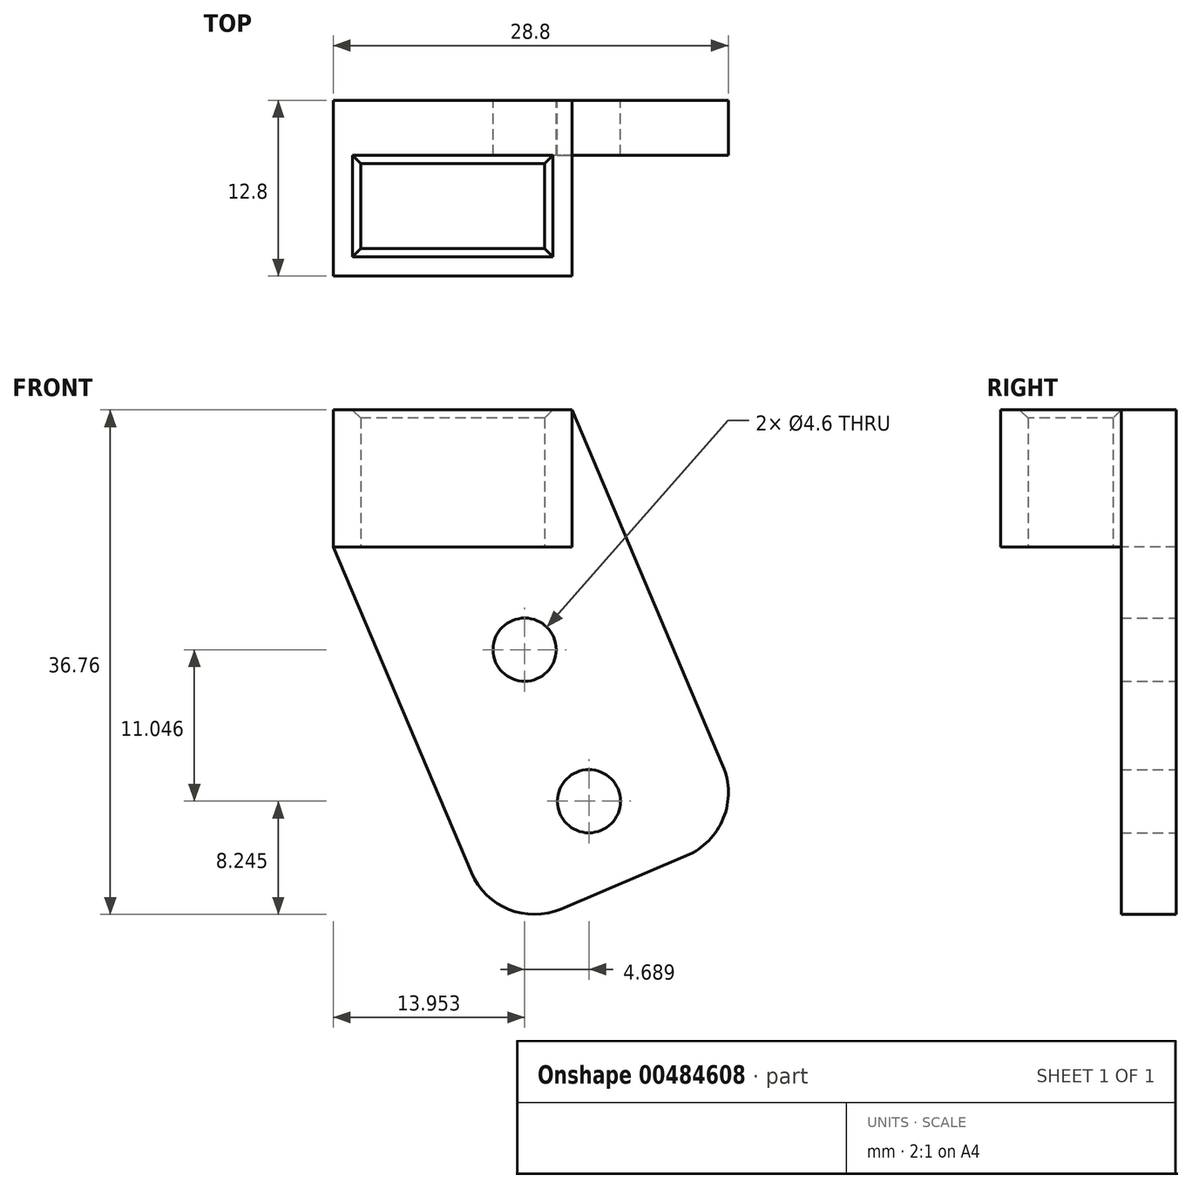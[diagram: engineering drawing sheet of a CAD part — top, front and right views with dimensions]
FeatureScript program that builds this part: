
annotation { "Feature Type Name" : "Feature", "Feature Type Description" : "" }
export const myFeature = defineFeature(function(context is Context, id is Id, definition is map)
    precondition{}
    {
        {
            var Q0;
            Q0=qCreatedBy(makeId("Top.planeOp"),FACE);
            var sketch = newSketch(context, id + "F0", { "sketchPlane" : qUnion([Q0])});
            skLineSegment(sketch, "E0.bottom", {"start": v(-12.09, 6.12) * mm, "end": v(1.31, 6.12) * mm});
            skLineSegment(sketch, "E0.top", {"start": v(-12.09, -0.08) * mm, "end": v(1.31, -0.08) * mm});
            skLineSegment(sketch, "E0.left", {"start": v(-12.09, 6.12) * mm, "end": v(-12.09, -0.08) * mm});
            skLineSegment(sketch, "E0.right", {"start": v(1.31, 6.12) * mm, "end": v(1.31, -0.08) * mm});
            skLineSegment(sketch, "E1.bottom", {"start": v(-14.09, 6.72) * mm, "end": v(3.31, 6.72) * mm});
            skLineSegment(sketch, "E1.top", {"start": v(-14.09, -2.08) * mm, "end": v(3.31, -2.08) * mm});
            skLineSegment(sketch, "E1.left", {"start": v(-14.09, 6.72) * mm, "end": v(-14.09, -2.08) * mm});
            skLineSegment(sketch, "E1.right", {"start": v(3.31, 6.72) * mm, "end": v(3.31, -2.08) * mm});
            skSolve(sketch);
        }
        {
            var Q0;
            Q0=qSketchRegion(id+"F0",true);
            var Q1;
            Q1=makeQuery(id+"F0.imprint","IMPRINT",FACE,{"disambiguationData":[TD([[makeQuery(id+"F0.imprint","IMPRINT",EDGE,{"derivedFrom":sQuery(id+"F0.wireOp",EDGE,"E0.bottom")}),1.0]])]});
            extrude(context, id + "F1", {"entities" : qUnion([Q0, Q1]), "depth" : 10 * mm, "offsetDistance" : 25 * mm});
        }
        {
            var Q0;
            Q0=makeQuery(id+"F1.opExtrude","SWEPT_FACE",FACE,{"disambiguationData":[OSD([sQuery(id+"F0.wireOp",EDGE,"E1.bottom")])]});
            var sketch = newSketch(context, id + "F2", { "sketchPlane" : qUnion([Q0])});
            skLineSegment(sketch, "E2", {"start": v(-3.31, 10) * mm, "end": v(-3.31, 10) * mm});
            skLineSegment(sketch, "E3", {"start": v(-3.31, 10) * mm, "end": v(-16.27, -20.53) * mm});
            skLineSegment(sketch, "E4", {"start": v(2.07, -28.32) * mm, "end": v(14.09, 0) * mm});
            skLineSegment(sketch, "E5", {"start": v(2.07, -28.32) * mm, "end": v(-16.27, -20.53) * mm});
            skPoint(sketch, "E6", {"position": v(0.14, -7.47) * mm});
            skPoint(sketch, "E7", {"position": v(-4.55, -18.52) * mm});
            skSolve(sketch);
        }
        {
            var Q0;
            {var subQ0=sQuery(id+"F2.wireOp",EDGE,"1mkYDBRP-PWp6-GeY6-MU8M-iDzXnznpOOjV.top");Q0=makeQuery(id+"F2.imprint","IMPRINT",FACE,{"disambiguationData":[TD([[makeQuery(id+"F2.imprint","IMPRINT",EDGE,{"derivedFrom":subQ0}),-1.0]])]});}
            var Q1;
            Q1=makeQuery(id+"F2.imprint","IMPRINT",FACE,{"disambiguationData":[TD([[makeQuery(id+"F2.imprint","IMPRINT",EDGE,{"derivedFrom":sQuery(id+"F2.wireOp",EDGE,"f9b377b0-091d-403c-b7d1-5019ea25e836.0.0")}),-1.0]])]});
            var Q2;
            Q2=makeQuery(id+"F2.imprint","IMPRINT",FACE,{"disambiguationData":[TD([[makeQuery(id+"F2.imprint","IMPRINT",EDGE,{"derivedFrom":sQuery(id+"F2.wireOp",EDGE,"E2")}),1.0]])]});
            var Q3;
            {var subQ0=sQuery(id+"F0.wireOp",EDGE,"E1.bottom");Q3=makeQuery(id+"F2.imprint","IMPRINT",FACE,{"disambiguationData":[TD([[makeQuery(id+"F2.imprint","IMPRINT",EDGE,{"derivedFrom":makeQuery(id+"F1.opExtrude","CAP_EDGE",EDGE,{"disambiguationData":[OSD([subQ0])],"isStart":true})}),-1.0]])]});}
            var Q4;
            Q4=makeQuery(id+"F2.imprint","IMPRINT",FACE,{"disambiguationData":[TD([[makeQuery(id+"F2.imprint","IMPRINT",EDGE,{"derivedFrom":sQuery(id+"F2.wireOp",EDGE,"E3")}),1.0]])]});
            extrude(context, id + "F3", {"entities" : qUnion([Q0, Q1, Q2, Q3, Q4]), "operationType" : NewBodyOperationType.ADD, "depth" : 4 * mm, "offsetDistance" : 25 * mm});
        }
        {
            var Q0;
            Q0=sQuery(id+"F2.wireOp",VERTEX,"E6");
            var Q1;
            Q1=sQuery(id+"F2.wireOp",VERTEX,"E7");
            var Q2;
            Q2=makeQuery(id+"F1.opExtrude","SWEPT_BODY",BODY,{"disambiguationData":[OSD([sQuery(id+"F0.wireOp",EDGE,"E0.bottom"),sQuery(id+"F0.wireOp",EDGE,"E0.top"),sQuery(id+"F0.wireOp",EDGE,"E0.left"),sQuery(id+"F0.wireOp",EDGE,"E0.right"),sQuery(id+"F0.wireOp",EDGE,"E1.bottom"),sQuery(id+"F0.wireOp",EDGE,"E1.top"),sQuery(id+"F0.wireOp",EDGE,"E1.left"),sQuery(id+"F0.wireOp",EDGE,"E1.right")])]});
            hole(context, id + "F4", {"style" : HoleStyle.SIMPLE, "endStyle" : HoleEndStyle.BLIND, "oppositeDirection" : true, "holeDiameter" : 4.6 * mm, "majorDiameter" : 5 * mm, "holeDepth" : 10 * mm, "isTappedThrough" : true, "tappedDepth" : 7 * mm, "tapClearance" : 6, "locations" : qUnion([Q0, Q1]), "scope" : qUnion([Q2]), "startStyle" : HoleStartStyle.SKETCH});
        }
        {
            var Q0;
            Q0=makeQuery(id+"F3.opExtrude","SWEPT_EDGE",EDGE,{"disambiguationData":[OSD([sQuery(id+"F2.wireOp",EDGE,"E3"),sQuery(id+"F2.wireOp",EDGE,"E5")])]});
            var Q1;
            Q1=makeQuery(id+"F3.opExtrude","SWEPT_EDGE",EDGE,{"disambiguationData":[OSD([sQuery(id+"F2.wireOp",EDGE,"E4"),sQuery(id+"F2.wireOp",EDGE,"E5")])]});
            fillet(context, id + "F5", {"entities" : qUnion([Q0, Q1]), "radius" : 5 * mm, "tangentPropagation" : true, "allowEdgeOverflow" : false});
        }
        {
            var Q0;
            Q0=makeQuery(id+"F1.opExtrude","CAP_EDGE",EDGE,{"disambiguationData":[OSD([sQuery(id+"F0.wireOp",EDGE,"E0.bottom")])],"isStart":false});
            var Q1;
            Q1=makeQuery(id+"F1.opExtrude","CAP_EDGE",EDGE,{"disambiguationData":[OSD([sQuery(id+"F0.wireOp",EDGE,"E0.right")])],"isStart":false});
            var Q2;
            Q2=makeQuery(id+"F1.opExtrude","CAP_EDGE",EDGE,{"disambiguationData":[OSD([sQuery(id+"F0.wireOp",EDGE,"E0.left")])],"isStart":false});
            var Q3;
            Q3=makeQuery(id+"F1.opExtrude","CAP_EDGE",EDGE,{"disambiguationData":[OSD([sQuery(id+"F0.wireOp",EDGE,"E0.top")])],"isStart":false});
            chamfer(context, id + "F6", {"entities" : qUnion([Q0, Q1, Q2, Q3]), "width" : 0.6 * mm, "tangentPropagation" : true});
        }
    });
